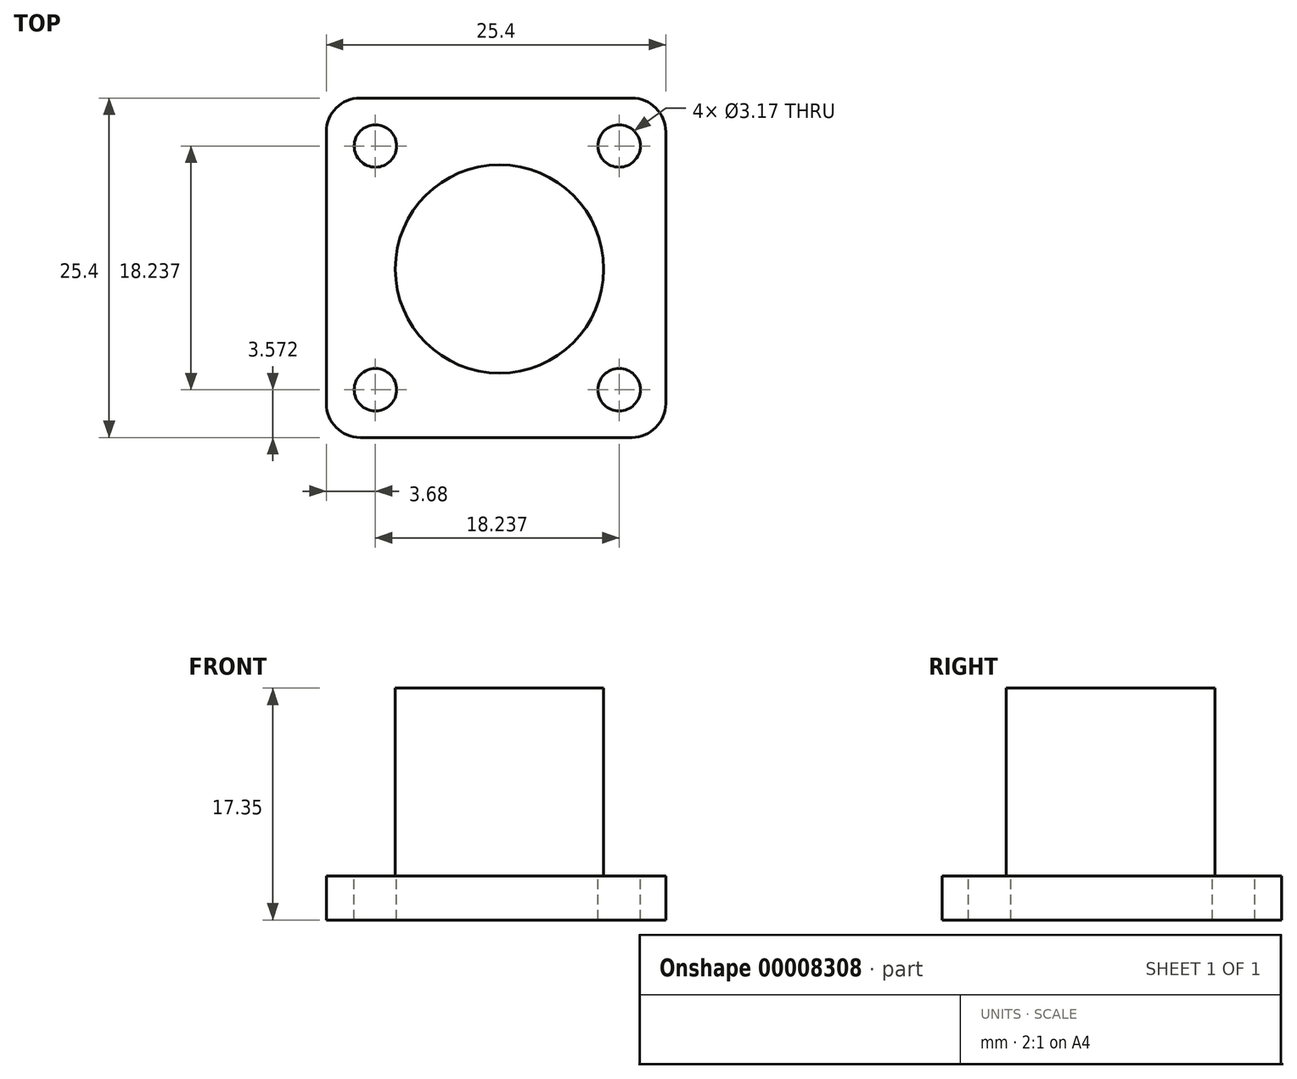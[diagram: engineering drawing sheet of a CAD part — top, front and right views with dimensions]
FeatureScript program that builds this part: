
annotation { "Feature Type Name" : "Feature", "Feature Type Description" : "" }
export const myFeature = defineFeature(function(context is Context, id is Id, definition is map)
    precondition{}
    {
        {
            var Q0;
            Q0=qCreatedBy(makeId("Top.planeOp"),FACE);
            var sketch = newSketch(context, id + "F0", { "sketchPlane" : qUnion([Q0])});
            skLineSegment(sketch, "E0.bottom", {"start": v(2.54, 0) * mm, "end": v(22.86, 0) * mm});
            skLineSegment(sketch, "E0.top", {"start": v(2.54, -25.4) * mm, "end": v(22.86, -25.4) * mm});
            skLineSegment(sketch, "E0.left", {"start": v(0, -2.54) * mm, "end": v(0, -22.86) * mm});
            skLineSegment(sketch, "E0.right", {"start": v(25.4, -2.54) * mm, "end": v(25.4, -22.86) * mm});
            skPoint(sketch, "E1.visualSharp", {"position": v(25.4, 0) * mm});
            skArc(sketch, "E1.filletArc", {"start": v(25.4, -2.54) * mm, "mid": v(24.66, -0.74) * mm, "end": v(22.86, 0) * mm});
            skPoint(sketch, "E2.visualSharp", {"position": v(25.4, -25.4) * mm});
            skArc(sketch, "E2.filletArc", {"start": v(22.86, -25.4) * mm, "mid": v(24.66, -24.66) * mm, "end": v(25.4, -22.86) * mm});
            skPoint(sketch, "E3.visualSharp", {"position": v(0, -25.4) * mm});
            skArc(sketch, "E3.filletArc", {"start": v(0, -22.86) * mm, "mid": v(0.74, -24.66) * mm, "end": v(2.54, -25.4) * mm});
            skPoint(sketch, "E4.visualSharp", {"position": v(0, 0) * mm});
            skArc(sketch, "E4.filletArc", {"start": v(2.54, 0) * mm, "mid": v(0.74, -0.74) * mm, "end": v(0, -2.54) * mm});
            skSolve(sketch);
        }
        {
            var Q0;
            Q0=makeQuery(id+"F0.imprint","IMPRINT",FACE,{"disambiguationData":[TD([[makeQuery(id+"F0.imprint","IMPRINT",EDGE,{"derivedFrom":sQuery(id+"F0.wireOp",EDGE,"E0.bottom")}),-1.0]])]});
            extrude(context, id + "F1", {"entities" : qUnion([Q0]), "depth" : 3.3 * mm});
        }
        {
            var Q0;
            Q0=makeQuery(id+"F1.opExtrude","CAP_FACE",FACE,{"disambiguationData":[OSD([sQuery(id+"F0.wireOp",EDGE,"E0.bottom"),sQuery(id+"F0.wireOp",EDGE,"E0.top"),sQuery(id+"F0.wireOp",EDGE,"E0.left"),sQuery(id+"F0.wireOp",EDGE,"E0.right"),sQuery(id+"F0.wireOp",EDGE,"E1.filletArc"),sQuery(id+"F0.wireOp",EDGE,"E2.filletArc"),sQuery(id+"F0.wireOp",EDGE,"E3.filletArc"),sQuery(id+"F0.wireOp",EDGE,"E4.filletArc")])],"isStart":false});
            var sketch = newSketch(context, id + "F2", { "sketchPlane" : qUnion([Q0])});
            skCircle(sketch, "E5", {"center": v(3.68, -21.83) * mm, "radius": 1.59 * mm});
            skCircle(sketch, "E6", {"center": v(21.92, -21.83) * mm, "radius": 1.59 * mm});
            skCircle(sketch, "E7", {"center": v(21.92, -3.6) * mm, "radius": 1.59 * mm});
            skCircle(sketch, "E8", {"center": v(3.68, -3.6) * mm, "radius": 1.59 * mm});
            skSolve(sketch);
        }
        {
            var Q0;
            Q0 = qSketchRegion(id + "F2", true);
            extrude(context, id + "F3", {"entities" : qUnion([Q0]), "operationType" : NewBodyOperationType.REMOVE, "endBound" : BoundingType.THROUGH_ALL, "oppositeDirection" : true, "depth" : 25.4 * mm});
        }
        {
            var Q0;
            Q0=makeQuery(id+"F1.opExtrude","CAP_FACE",FACE,{"disambiguationData":[OSD([sQuery(id+"F0.wireOp",EDGE,"E0.bottom"),sQuery(id+"F0.wireOp",EDGE,"E0.top"),sQuery(id+"F0.wireOp",EDGE,"E0.left"),sQuery(id+"F0.wireOp",EDGE,"E0.right"),sQuery(id+"F0.wireOp",EDGE,"E1.filletArc"),sQuery(id+"F0.wireOp",EDGE,"E2.filletArc"),sQuery(id+"F0.wireOp",EDGE,"E3.filletArc"),sQuery(id+"F0.wireOp",EDGE,"E4.filletArc")])],"isStart":false});
            var sketch = newSketch(context, id + "F4", { "sketchPlane" : qUnion([Q0])});
            skCircle(sketch, "E9", {"center": v(12.96, -12.8) * mm, "radius": 7.8 * mm});
            skSolve(sketch);
        }
        {
            var Q0;
            Q0=makeQuery(id+"F4.imprint","IMPRINT",FACE,{"disambiguationData":[TD([[makeQuery(id+"F4.imprint","IMPRINT",EDGE,{"derivedFrom":sQuery(id+"F4.wireOp",EDGE,"E9")}),1.0]])]});
            extrude(context, id + "F5", {"entities" : qUnion([Q0]), "operationType" : NewBodyOperationType.ADD, "depth" : 14.05 * mm});
        }
    });
